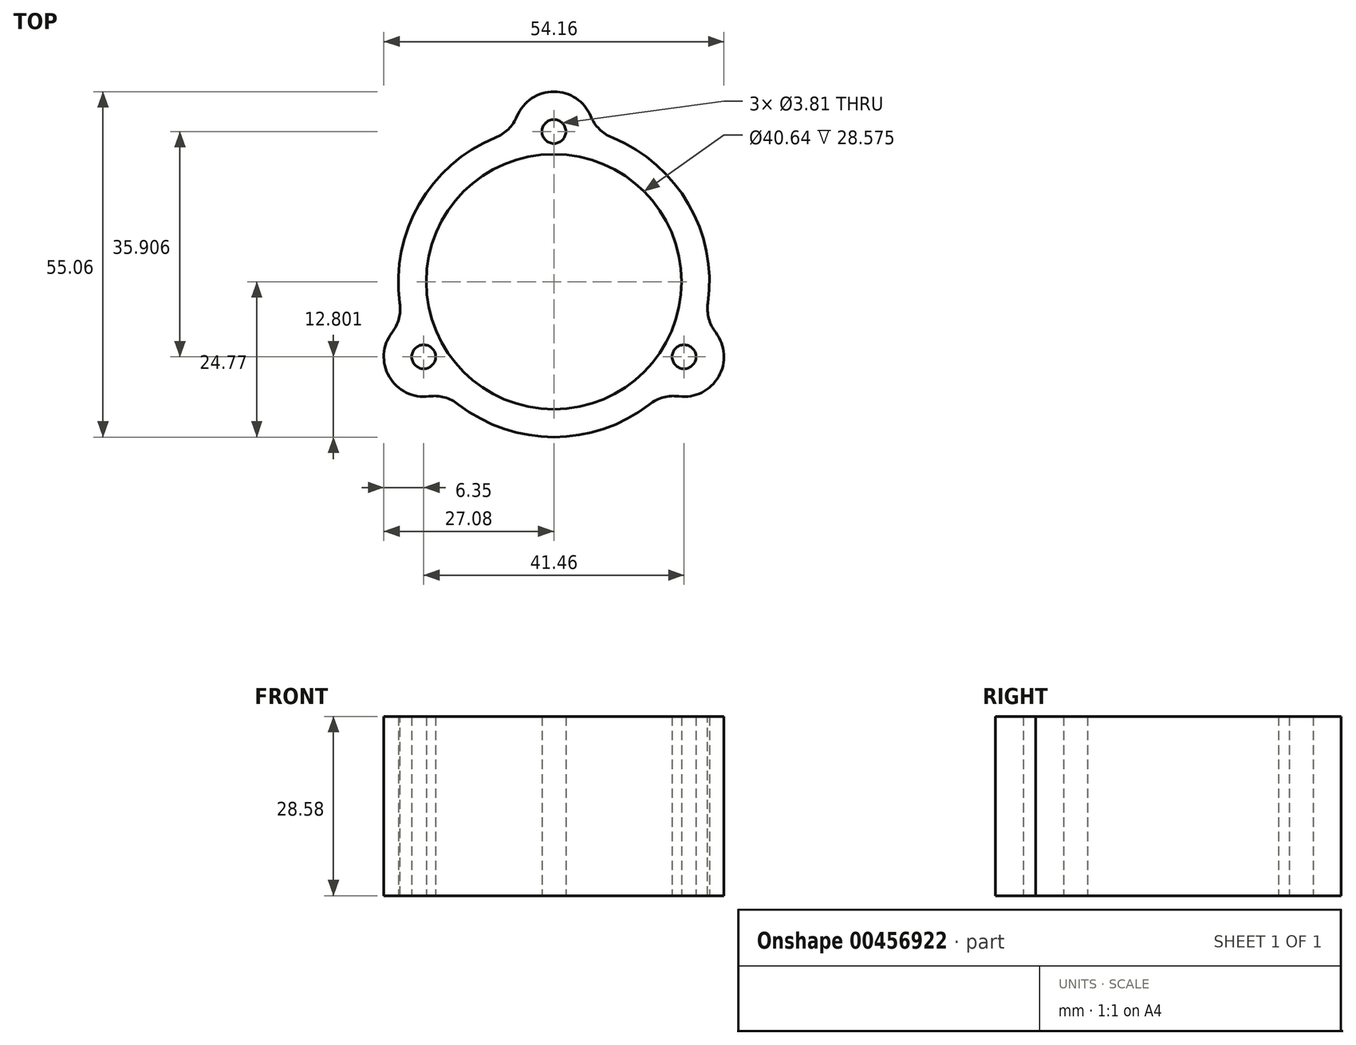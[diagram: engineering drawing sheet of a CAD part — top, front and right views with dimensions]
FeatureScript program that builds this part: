
annotation { "Feature Type Name" : "Feature", "Feature Type Description" : "" }
export const myFeature = defineFeature(function(context is Context, id is Id, definition is map)
    precondition{}
    {
        {
            var Q0;
            Q0=qCreatedBy(makeId("Top.planeOp"),FACE);
            var sketch = newSketch(context, id + "F0", { "sketchPlane" : qUnion([Q0])});
            skCircle(sketch, "E0", {"center": v(0, 0) * mm, "radius": 20.32 * mm});
            skCircle(sketch, "E1", {"center": v(0, 0) * mm, "radius": 24.77 * mm});
            skLineSegment(sketch, "E2", {"start": v(0, 0) * mm, "end": v(0, 42.77) * mm, "construction": true});
            skLineSegment(sketch, "E3", {"start": v(0, 0) * mm, "end": v(-43.71, -25.24) * mm, "construction": true});
            skLineSegment(sketch, "E4", {"start": v(0, 0) * mm, "end": v(46.9, -27.08) * mm, "construction": true});
            skLineSegment(sketch, "E5", {"start": v(-6.35, 2.16) * mm, "end": v(-6.35, 48.97) * mm, "construction": true});
            skLineSegment(sketch, "E6.MirrorCS", {"start": v(6.35, 2.16) * mm, "end": v(6.35, 48.97) * mm, "construction": true});
            skLineSegment(sketch, "E7", {"start": v(-11.23, 0.85) * mm, "end": v(-48.99, -20.95) * mm, "construction": true});
            skLineSegment(sketch, "E8.MirrorCS", {"start": v(-4.88, -10.15) * mm, "end": v(-42.64, -31.95) * mm, "construction": true});
            skLineSegment(sketch, "E9", {"start": v(0.14, -7.41) * mm, "end": v(38.48, -29.55) * mm, "construction": true});
            skLineSegment(sketch, "E10.MirrorCS", {"start": v(6.49, 3.59) * mm, "end": v(44.83, -18.55) * mm, "construction": true});
            skArc(sketch, "E11", {"start": v(6.35, 23.94) * mm, "mid": v(0, 30.29) * mm, "end": v(-6.35, 23.94) * mm});
            skArc(sketch, "E12", {"start": v(-23.9, -6.47) * mm, "mid": v(-26.23, -15.14) * mm, "end": v(-17.56, -17.47) * mm});
            skArc(sketch, "E13", {"start": v(17.56, -17.47) * mm, "mid": v(26.23, -15.14) * mm, "end": v(23.9, -6.47) * mm});
            skCircle(sketch, "E14", {"center": v(0, 23.94) * mm, "radius": 1.9 * mm});
            skCircle(sketch, "E15", {"center": v(-20.73, -11.97) * mm, "radius": 1.9 * mm});
            skCircle(sketch, "E16", {"center": v(20.73, -11.97) * mm, "radius": 1.9 * mm});
            skSolve(sketch);
        }
        {
            var Q0;
            Q0=makeQuery(id+"F0.imprint","IMPRINT",FACE,{"disambiguationData":[TD([[makeQuery(id+"F0.imprint","IMPRINT",EDGE,{"derivedFrom":sQuery(id+"F0.wireOp",EDGE,"E0")}),-1.0]])]});
            var Q1;
            {var subQ0=sQuery(id+"F0.wireOp",EDGE,"E12");Q1=makeQuery(id+"F0.imprint","IMPRINT",FACE,{"disambiguationData":[TD([[makeQuery(id+"F0.imprint","IMPRINT",EDGE,{"derivedFrom":subQ0}),1.0]])]});}
            var Q2;
            {var subQ0=sQuery(id+"F0.wireOp",EDGE,"E11");Q2=makeQuery(id+"F0.imprint","IMPRINT",FACE,{"disambiguationData":[TD([[makeQuery(id+"F0.imprint","IMPRINT",EDGE,{"derivedFrom":subQ0}),1.0]])]});}
            var Q3;
            {var subQ0=sQuery(id+"F0.wireOp",EDGE,"E13");Q3=makeQuery(id+"F0.imprint","IMPRINT",FACE,{"disambiguationData":[TD([[makeQuery(id+"F0.imprint","IMPRINT",EDGE,{"derivedFrom":subQ0}),1.0]])]});}
            extrude(context, id + "F1", {"entities" : qUnion([Q0, Q1, Q2, Q3]), "depth" : 28.57 * mm});
        }
        {
            var Q0;
            {var subQ0=sQuery(id+"F0.wireOp",EDGE,"E11");var subQ1=sQuery(id+"F0.wireOp",EDGE,"E1");Q0=makeQuery(id+"F1.opExtrude","SWEPT_EDGE",EDGE,{"disambiguationData":[OSD([subQ1,subQ0]),TDD([makeQuery(id+"F0.imprint","INTERSECT",VERTEX,{"disambiguationData":[OD(1.0)],"derivedFrom":[subQ1,subQ0]})])]});}
            var Q1;
            {var subQ0=sQuery(id+"F0.wireOp",EDGE,"E12");var subQ1=sQuery(id+"F0.wireOp",EDGE,"E1");Q1=makeQuery(id+"F1.opExtrude","SWEPT_EDGE",EDGE,{"disambiguationData":[OSD([subQ1,subQ0]),TDD([makeQuery(id+"F0.imprint","INTERSECT",VERTEX,{"disambiguationData":[OD(0.0)],"derivedFrom":[subQ1,subQ0]})])]});}
            var Q2;
            {var subQ0=sQuery(id+"F0.wireOp",EDGE,"E12");var subQ1=sQuery(id+"F0.wireOp",EDGE,"E1");Q2=makeQuery(id+"F1.opExtrude","SWEPT_EDGE",EDGE,{"disambiguationData":[OSD([subQ1,subQ0]),TDD([makeQuery(id+"F0.imprint","INTERSECT",VERTEX,{"disambiguationData":[OD(1.0)],"derivedFrom":[subQ1,subQ0]})])]});}
            var Q3;
            {var subQ0=sQuery(id+"F0.wireOp",EDGE,"E13");var subQ1=sQuery(id+"F0.wireOp",EDGE,"E1");Q3=makeQuery(id+"F1.opExtrude","SWEPT_EDGE",EDGE,{"disambiguationData":[OSD([subQ1,subQ0]),TDD([makeQuery(id+"F0.imprint","INTERSECT",VERTEX,{"disambiguationData":[OD(0.0)],"derivedFrom":[subQ1,subQ0]})])]});}
            var Q4;
            {var subQ0=sQuery(id+"F0.wireOp",EDGE,"E13");var subQ1=sQuery(id+"F0.wireOp",EDGE,"E1");Q4=makeQuery(id+"F1.opExtrude","SWEPT_EDGE",EDGE,{"disambiguationData":[OSD([subQ1,subQ0]),TDD([makeQuery(id+"F0.imprint","INTERSECT",VERTEX,{"disambiguationData":[OD(1.0)],"derivedFrom":[subQ1,subQ0]})])]});}
            var Q5;
            {var subQ0=sQuery(id+"F0.wireOp",EDGE,"E11");var subQ1=sQuery(id+"F0.wireOp",EDGE,"E1");Q5=makeQuery(id+"F1.opExtrude","SWEPT_EDGE",EDGE,{"disambiguationData":[OSD([subQ1,subQ0]),TDD([makeQuery(id+"F0.imprint","INTERSECT",VERTEX,{"disambiguationData":[OD(0.0)],"derivedFrom":[subQ1,subQ0]})])]});}
            fillet(context, id + "F2", {"entities" : qUnion([Q0, Q1, Q2, Q3, Q4, Q5]), "radius" : 6.35 * mm, "tangentPropagation" : true, "allowEdgeOverflow" : false});
        }
    });
